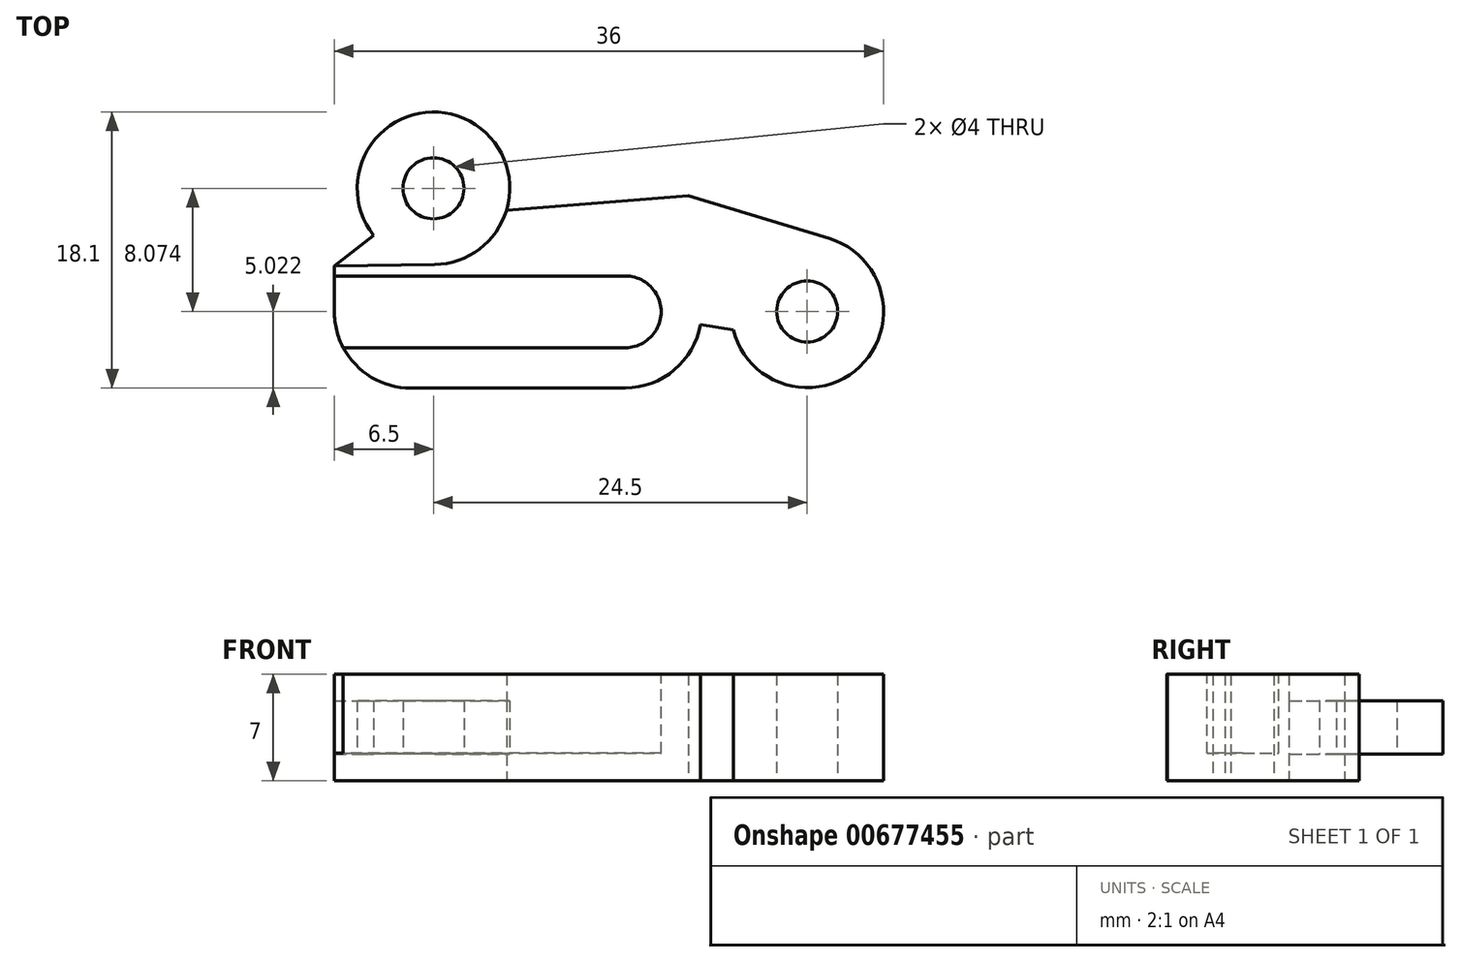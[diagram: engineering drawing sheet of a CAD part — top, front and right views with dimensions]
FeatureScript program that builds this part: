
annotation { "Feature Type Name" : "Feature", "Feature Type Description" : "" }
export const myFeature = defineFeature(function(context is Context, id is Id, definition is map)
    precondition{}
    {
        {
            var Q0;
            Q0=qCreatedBy(makeId("Top.planeOp"),FACE);
            var sketch = newSketch(context, id + "F0", { "sketchPlane" : qUnion([Q0])});
            skLineSegment(sketch, "E0", {"start": v(19, 0) * mm, "end": v(4.94, -0.01) * mm});
            skLineSegment(sketch, "E1", {"start": v(-0.07, 4.99) * mm, "end": v(-0.07, 7.99) * mm});
            skPoint(sketch, "E2", {"position": v(30.93, 0.01) * mm});
            skPoint(sketch, "E3", {"position": v(30.93, 5.01) * mm});
            skArc(sketch, "E4", {"start": v(26.08, 3.8) * mm, "mid": v(34.38, 1.39) * mm, "end": v(32.38, 9.8) * mm});
            skArc(sketch, "E5.filletArc", {"start": v(-0.07, 4.99) * mm, "mid": v(1.4, 1.45) * mm, "end": v(4.94, -0.01) * mm});
            skArc(sketch, "E6.filletArc", {"start": v(19, 0) * mm, "mid": v(22.23, 1.18) * mm, "end": v(23.93, 4.17) * mm});
            skPoint(sketch, "E7", {"position": v(6.43, 13.09) * mm});
            skArc(sketch, "E8", {"start": v(11.22, 11.66) * mm, "mid": v(5.5, 18) * mm, "end": v(2.5, 10) * mm});
            skCircle(sketch, "E9", {"center": v(6.43, 13.09) * mm, "radius": 2 * mm});
            skCircle(sketch, "E10", {"center": v(30.93, 5.01) * mm, "radius": 2 * mm});
            skLineSegment(sketch, "E11.trimOffspring", {"start": v(11.22, 11.66) * mm, "end": v(23.13, 12.6) * mm});
            skPoint(sketch, "E12", {"position": v(23.13, 12.6) * mm});
            skLineSegment(sketch, "E13", {"start": v(23.13, 12.6) * mm, "end": v(32.38, 9.8) * mm});
            skPoint(sketch, "E14", {"position": v(-0.07, 7.99) * mm});
            skLineSegment(sketch, "E15", {"start": v(23.93, 4.17) * mm, "end": v(26.08, 3.8) * mm});
            skLineSegment(sketch, "E16", {"start": v(-0.07, 7.99) * mm, "end": v(2.5, 10) * mm});
            skSolve(sketch);
        }
        {
            var Q0;
            Q0=makeQuery(id+"F0.imprint","IMPRINT",FACE,{"disambiguationData":[TD([[makeQuery(id+"F0.imprint","IMPRINT",EDGE,{"derivedFrom":sQuery(id+"F0.wireOp",EDGE,"E0")}),-1.0]])]});
            extrude(context, id + "F1", {"entities" : qUnion([Q0]), "depth" : 7 * mm, "offsetDistance" : 25 * mm});
        }
        {
            var Q0;
            Q0=makeQuery(id+"F1.opExtrude","CAP_FACE",FACE,{"disambiguationData":[OSD([sQuery(id+"F0.wireOp",EDGE,"E0"),sQuery(id+"F0.wireOp",EDGE,"E1"),sQuery(id+"F0.wireOp",EDGE,"E4"),sQuery(id+"F0.wireOp",EDGE,"E5.filletArc"),sQuery(id+"F0.wireOp",EDGE,"E6.filletArc"),sQuery(id+"F0.wireOp",EDGE,"E8"),sQuery(id+"F0.wireOp",EDGE,"E9"),sQuery(id+"F0.wireOp",EDGE,"E10"),sQuery(id+"F0.wireOp",EDGE,"E11.trimOffspring"),sQuery(id+"F0.wireOp",EDGE,"E13"),sQuery(id+"F0.wireOp",EDGE,"qW6NsB8J-Pp6Y-0HLB-6KF8-abTtBDbUBjve"),sQuery(id+"F0.wireOp",EDGE,"E15")])],"isStart":false});
            var sketch = newSketch(context, id + "F2", { "sketchPlane" : qUnion([Q0])});
            skPoint(sketch, "E17", {"position": v(-0.07, 7.34) * mm});
            skLineSegment(sketch, "E18", {"start": v(-0.07, 7.34) * mm, "end": v(19, 7.34) * mm});
            skArc(sketch, "E19", {"start": v(19, 2.64) * mm, "mid": v(21.35, 4.99) * mm, "end": v(19, 7.34) * mm});
            skLineSegment(sketch, "E20", {"start": v(19, 2.64) * mm, "end": v(0.52, 2.64) * mm});
            skSolve(sketch);
        }
        {
            var Q0;
            {var subQ3=sQuery(id+"F2.wireOp",EDGE,"E18");Q0=makeQuery(id+"F2.imprint","IMPRINT",FACE,{"disambiguationData":[TD([[makeQuery(id+"F2.imprint","IMPRINT",EDGE,{"derivedFrom":subQ3}),-1.0]])]});}
            extrude(context, id + "F3", {"entities" : qUnion([Q0]), "operationType" : NewBodyOperationType.REMOVE, "depth" : -5.2 * mm, "offsetDistance" : 25 * mm});
        }
        {
            var Q0;
            Q0=makeQuery(id+"F0.imprint","IMPRINT",FACE,{"disambiguationData":[TD([[makeQuery(id+"F0.imprint","IMPRINT",EDGE,{"derivedFrom":sQuery(id+"F0.wireOp",EDGE,"E0")}),-1.0]])]});
            var sketch = newSketch(context, id + "F4", { "sketchPlane" : qUnion([Q0])});
            skArc(sketch, "E21", {"start": v(6.5, 8.09) * mm, "mid": v(8.59, 17.6) * mm, "end": v(2.5, 10) * mm});
            skLineSegment(sketch, "E22", {"start": v(6.5, 8.09) * mm, "end": v(-0.07, 8) * mm});
            skLineSegment(sketch, "E23", {"start": v(-0.07, 8) * mm, "end": v(2.5, 10) * mm});
            skSolve(sketch);
        }
        {
            var Q0;
            Q0=makeQuery(id+"F4.imprint","IMPRINT",FACE,{"disambiguationData":[TD([[makeQuery(id+"F4.imprint","IMPRINT",EDGE,{"derivedFrom":makeQuery(id+"F0.imprint","IMPRINT",EDGE,{"derivedFrom":sQuery(id+"F0.wireOp",EDGE,"E9")})}),-1.0]])]});
            extrude(context, id + "F5", {"entities" : qUnion([Q0]), "operationType" : NewBodyOperationType.REMOVE, "depth" : 1.75 * mm, "offsetDistance" : 25 * mm});
        }
        {
            var Q0;
            Q0=makeQuery(id+"F1.opExtrude","CAP_FACE",FACE,{"disambiguationData":[OSD([sQuery(id+"F0.wireOp",EDGE,"E0"),sQuery(id+"F0.wireOp",EDGE,"E1"),sQuery(id+"F0.wireOp",EDGE,"E4"),sQuery(id+"F0.wireOp",EDGE,"E5.filletArc"),sQuery(id+"F0.wireOp",EDGE,"E6.filletArc"),sQuery(id+"F0.wireOp",EDGE,"E8"),sQuery(id+"F0.wireOp",EDGE,"E9"),sQuery(id+"F0.wireOp",EDGE,"E10"),sQuery(id+"F0.wireOp",EDGE,"E11.trimOffspring"),sQuery(id+"F0.wireOp",EDGE,"E13"),sQuery(id+"F0.wireOp",EDGE,"E15"),sQuery(id+"F0.wireOp",EDGE,"E16")])],"isStart":false});
            var sketch = newSketch(context, id + "F6", { "sketchPlane" : qUnion([Q0])});
            skArc(sketch, "E24", {"start": v(6.5, 8.09) * mm, "mid": v(8.58, 17.6) * mm, "end": v(2.5, 10) * mm});
            skLineSegment(sketch, "E25", {"start": v(-0.07, 7.99) * mm, "end": v(6.5, 8.09) * mm});
            skLineSegment(sketch, "E26", {"start": v(-0.07, 7.99) * mm, "end": v(2.5, 10) * mm});
            skSolve(sketch);
        }
        {
            var Q0;
            Q0 = qSketchRegion(id + "F6", true);
            extrude(context, id + "F7", {"entities" : qUnion([Q0]), "operationType" : NewBodyOperationType.REMOVE, "oppositeDirection" : true, "depth" : 1.75 * mm, "offsetDistance" : 25 * mm});
        }
    });
